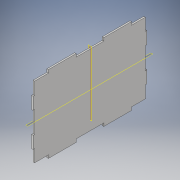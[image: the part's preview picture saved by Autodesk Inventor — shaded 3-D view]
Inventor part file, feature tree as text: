
AUTODESK INVENTOR PART (.ipt)
format: ipt  version: 2017 (Build 210142000, 142)  size: 157,696 bytes
history: native  units: in
note: dims shown in document units (in); Inventor stores cm internally (conversion verified against a paired STEP export)
features: extrude x3, sketch x3, plane x2, mirror x2, projected_geometry x1
ambient origin geometry x8: Origin, YZ Plane, XZ Plane, XY Plane, X Axis, Y Axis, Z Axis, Center Point
bodies: Solid1 (feature_tree)
feature tree (11):
  extrude  "Extrusion1"  Depth=72.0in
  extrude  "Extrusion2"  Depth=9.0in
  extrude  "Extrusion3"  Depth=2.0in TaperAngle=0.0deg
  plane  "Work Plane1"
  mirror  "Mirror1"
  plane  "Work Plane2"
  mirror  "Mirror2"
  sketch  "Sketch1"  dims[d0=46.0in d1=72.0in]
  sketch  "Sketch2"  dims[d2=1.0in d3=0.0in d4=9.0in]
  sketch  "Sketch3"  dims[d5=18.0in d6=2.0in d7=0.0in d8=8.0in d9=8.0in d10=1.0in d11=0.0in d12=8.0in d13=14.0in]
  projected_geometry  "Projected Loop1"
